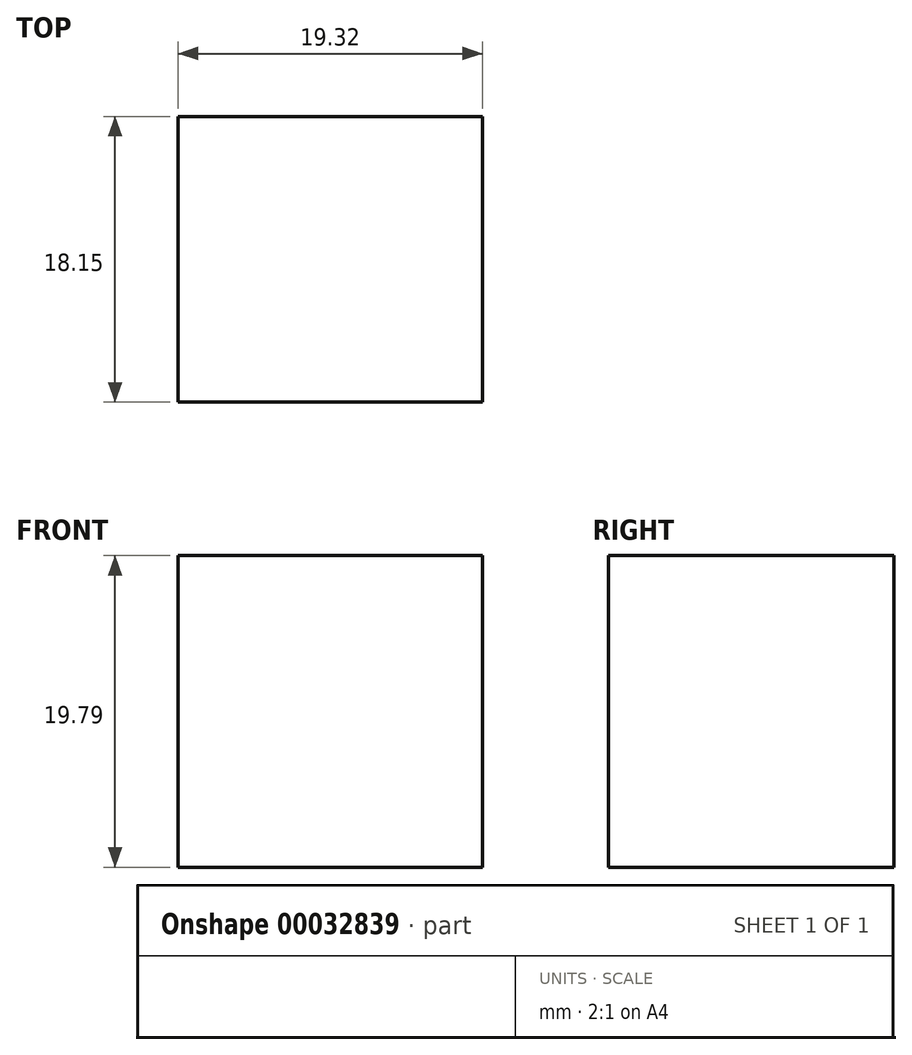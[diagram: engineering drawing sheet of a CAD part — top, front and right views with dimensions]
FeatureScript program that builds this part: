
annotation { "Feature Type Name" : "Feature", "Feature Type Description" : "" }
export const myFeature = defineFeature(function(context is Context, id is Id, definition is map)
    precondition{}
    {
        {
            var Q0;
            Q0=qCreatedBy(makeId("Front.planeOp"),FACE);
            var sketch = newSketch(context, id + "F0", { "sketchPlane" : qUnion([Q0])});
            skLineSegment(sketch, "E0.bottom", {"start": v(0, 0) * mm, "end": v(19.32, 0) * mm});
            skLineSegment(sketch, "E0.top", {"start": v(0, 19.79) * mm, "end": v(19.32, 19.79) * mm});
            skLineSegment(sketch, "E0.left", {"start": v(0, 0) * mm, "end": v(0, 19.79) * mm});
            skLineSegment(sketch, "E0.right", {"start": v(19.32, 0) * mm, "end": v(19.32, 19.79) * mm});
            skSolve(sketch);
        }
        {
            var Q0;
            Q0 = qSketchRegion(id + "F0", true);
            extrude(context, id + "F1", {"entities" : qUnion([Q0]), "oppositeDirection" : true, "depth" : 18.15 * mm});
        }
    });
